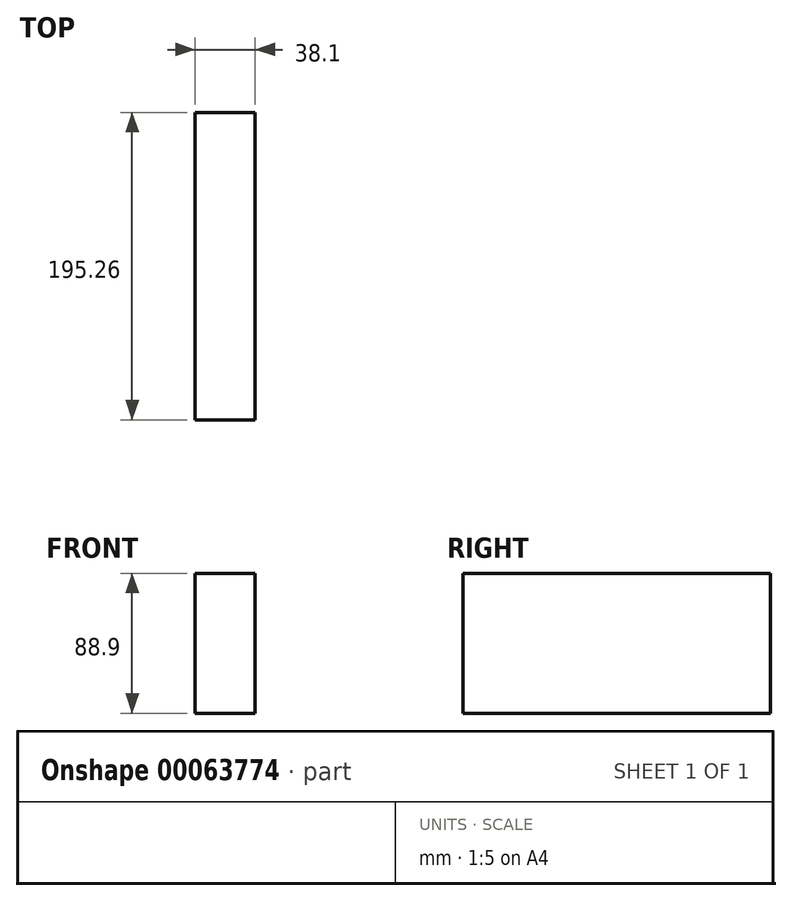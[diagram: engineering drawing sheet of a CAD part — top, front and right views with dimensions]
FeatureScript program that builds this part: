
annotation { "Feature Type Name" : "Feature", "Feature Type Description" : "" }
export const myFeature = defineFeature(function(context is Context, id is Id, definition is map)
    precondition{}
    {
        {
            var Q0;
            Q0=qCreatedBy(makeId("Front.planeOp"),FACE);
            var sketch = newSketch(context, id + "F0", { "sketchPlane" : qUnion([Q0])});
            skLineSegment(sketch, "E0.bottom", {"start": v(-18, 55.77) * mm, "end": v(20.1, 55.77) * mm});
            skLineSegment(sketch, "E0.top", {"start": v(-18, -33.13) * mm, "end": v(20.1, -33.13) * mm});
            skLineSegment(sketch, "E0.left", {"start": v(-18, 55.77) * mm, "end": v(-18, -33.13) * mm});
            skLineSegment(sketch, "E0.right", {"start": v(20.1, 55.77) * mm, "end": v(20.1, -33.13) * mm});
            skSolve(sketch);
        }
        {
            var Q0;
            Q0=qSketchRegion(id+"F0",true);
            extrude(context, id + "F1", {"entities" : qUnion([Q0]), "endBound" : BoundingType.SYMMETRIC, "depth" : 195.26 * mm});
        }
    });
